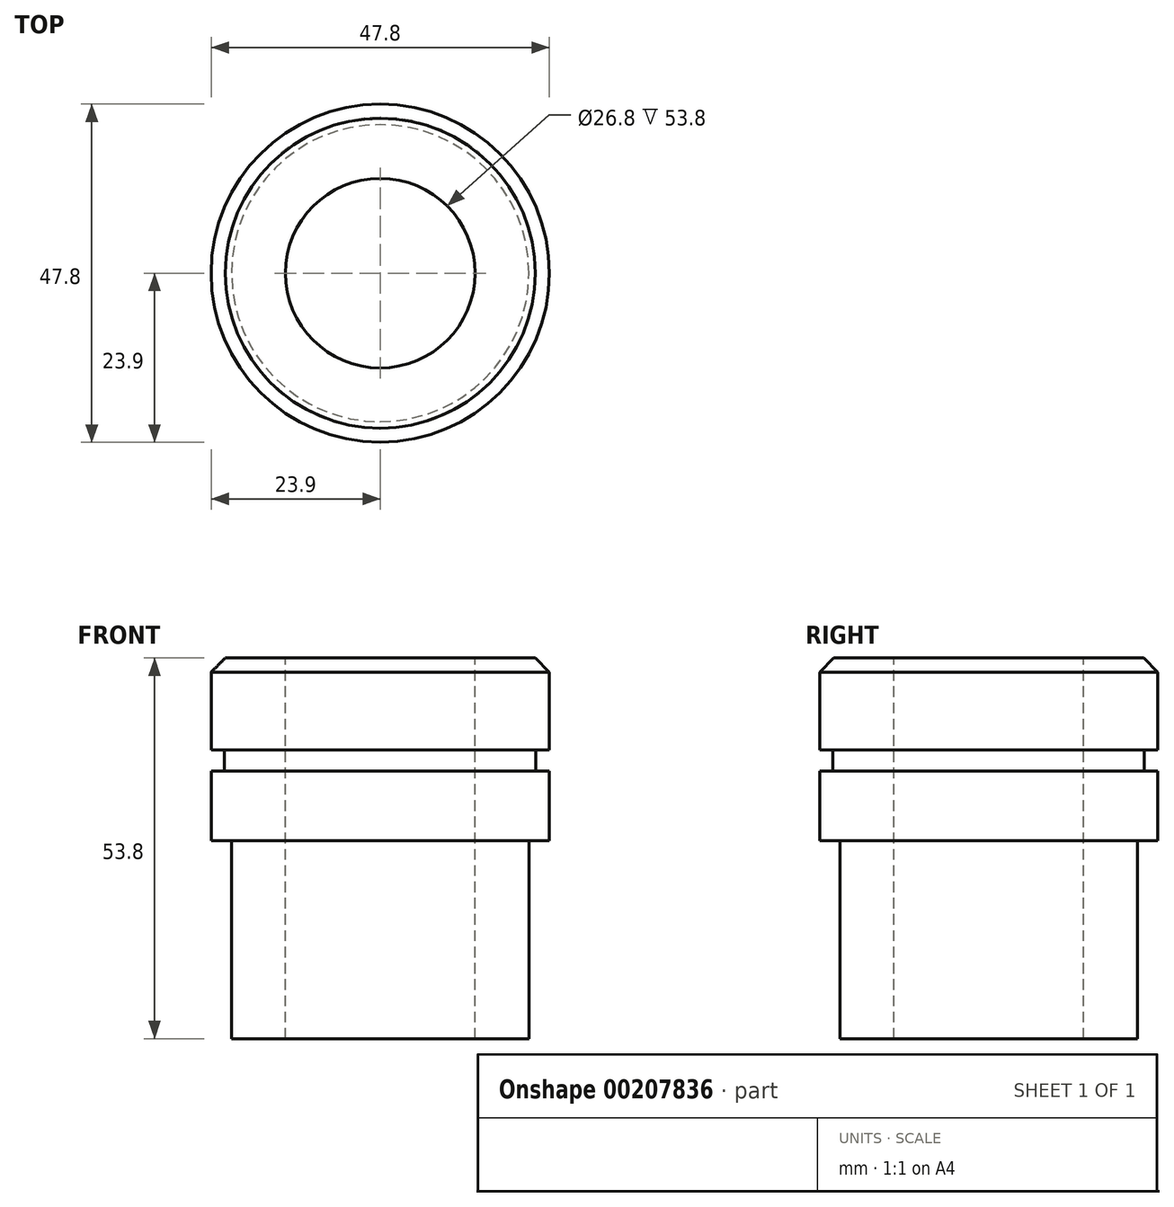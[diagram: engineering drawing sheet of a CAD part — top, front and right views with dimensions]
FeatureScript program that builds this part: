
annotation { "Feature Type Name" : "Feature", "Feature Type Description" : "" }
export const myFeature = defineFeature(function(context is Context, id is Id, definition is map)
    precondition{}
    {
        {
            var Q0;
            Q0=qCreatedBy(makeId("Front.planeOp"),FACE);
            var sketch = newSketch(context, id + "F0", { "sketchPlane" : qUnion([Q0])});
            skLineSegment(sketch, "E0", {"start": v(-21, 28) * mm, "end": v(-23.9, 28) * mm});
            skLineSegment(sketch, "E1", {"start": v(-23.9, 28) * mm, "end": v(-23.9, 37.8) * mm});
            skLineSegment(sketch, "E2", {"start": v(-23.9, 37.8) * mm, "end": v(-22, 37.8) * mm});
            skLineSegment(sketch, "E3", {"start": v(-22, 37.8) * mm, "end": v(-22, 40.8) * mm});
            skLineSegment(sketch, "E4", {"start": v(-22, 40.8) * mm, "end": v(-23.9, 40.8) * mm});
            skLineSegment(sketch, "E5", {"start": v(-23.9, 40.8) * mm, "end": v(-23.9, 53.8) * mm});
            skLineSegment(sketch, "E6", {"start": v(-23.9, 53.8) * mm, "end": v(-13.4, 53.8) * mm});
            skLineSegment(sketch, "E7", {"start": v(-13.4, 53.8) * mm, "end": v(-13.4, 0) * mm});
            skLineSegment(sketch, "E8", {"start": v(0, 20.6) * mm, "end": v(0, -9.26) * mm});
            skLineSegment(sketch, "E9", {"start": v(-21, 28) * mm, "end": v(-21, 0) * mm});
            skLineSegment(sketch, "E10", {"start": v(-21, 0) * mm, "end": v(-13.4, 0) * mm});
            skSolve(sketch);
        }
        {
            var Q0;
            Q0 = qSketchRegion(id + "F0", true);
            var Q1;
            Q1=sQuery(id+"F0.wireOp",EDGE,"E8");
            revolve(context, id + "F1", {"entities" : qUnion([Q0]), "axis" : qUnion([Q1]), "revolveType" : RevolveType.FULL});
        }
        {
            var Q0;
            Q0=makeQuery(id+"F1.opRevolve","SWEPT_EDGE",EDGE,{"disambiguationData":[OSD([sQuery(id+"F0.wireOp",EDGE,"E5"),sQuery(id+"F0.wireOp",EDGE,"E6")])]});
            chamfer(context, id + "F2", {"entities" : qUnion([Q0]), "width" : 2 * mm, "tangentPropagation" : true});
        }
    });
